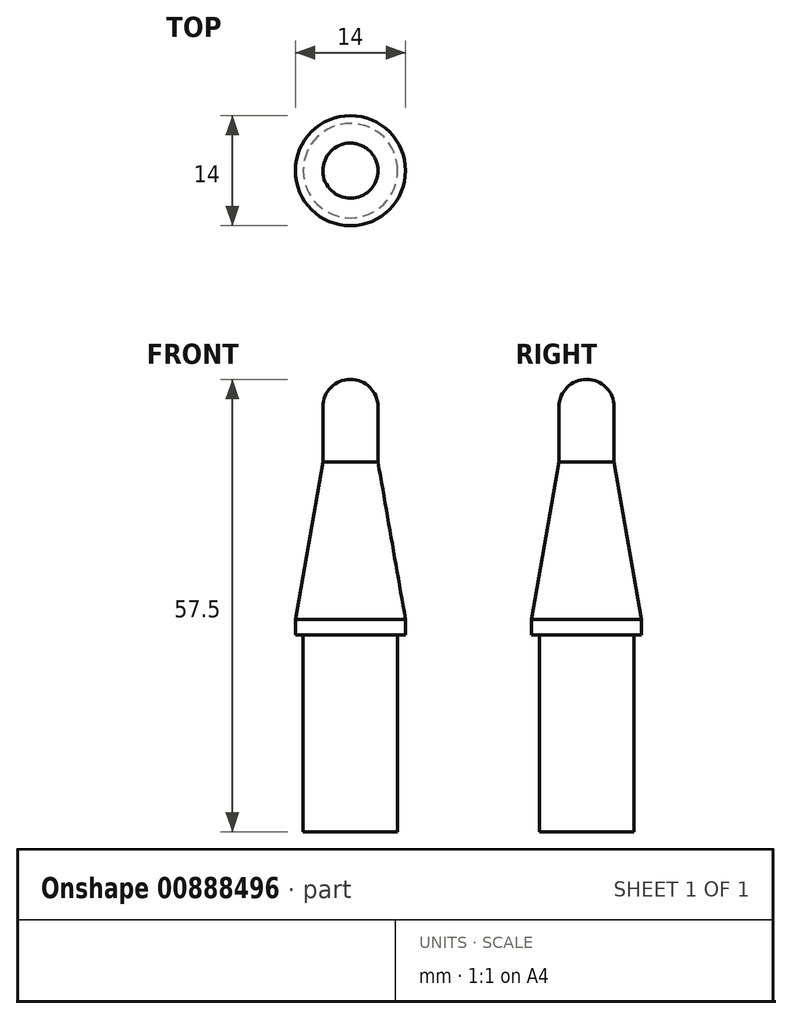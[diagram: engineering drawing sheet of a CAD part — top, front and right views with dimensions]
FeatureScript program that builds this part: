
annotation { "Feature Type Name" : "Feature", "Feature Type Description" : "" }
export const myFeature = defineFeature(function(context is Context, id is Id, definition is map)
    precondition{}
    {
        {
            var Q0;
            Q0=qCreatedBy(makeId("Top.planeOp"),FACE);
            var sketch = newSketch(context, id + "F0", { "sketchPlane" : qUnion([Q0])});
            skCircle(sketch, "E0", {"center": v(0, 0) * mm, "radius": 6 * mm});
            skSolve(sketch);
        }
        {
            var Q0;
            Q0 = qSketchRegion(id + "F0", true);
            extrude(context, id + "F1", {"entities" : qUnion([Q0]), "depth" : 25 * mm, "offsetDistance" : 25 * mm});
        }
        {
            var Q0;
            Q0=makeQuery(id+"F1.opExtrude","CAP_FACE",FACE,{"disambiguationData":[OSD([sQuery(id+"F0.wireOp",EDGE,"E0")])],"isStart":false});
            var sketch = newSketch(context, id + "F2", { "sketchPlane" : qUnion([Q0])});
            skCircle(sketch, "E1", {"center": v(0, 0) * mm, "radius": 7 * mm});
            skSolve(sketch);
        }
        {
            var Q0;
            Q0 = qSketchRegion(id + "F2", true);
            extrude(context, id + "F3", {"entities" : qUnion([Q0]), "operationType" : NewBodyOperationType.ADD, "depth" : 2 * mm, "offsetDistance" : 25 * mm});
        }
        {
            var Q0;
            Q0=makeQuery(id+"F3.opExtrude","CAP_FACE",FACE,{"disambiguationData":[OSD([sQuery(id+"F2.wireOp",EDGE,"E1")])],"isStart":false});
            cPlane(context, id + "F4", {"entities" : qUnion([Q0]), "cplaneType" : CPlaneType.OFFSET, "offset" : 20 * mm, "width" : 150 * mm, "height" : 150 * mm});
        }
        {
            var Q0;
            Q0=qCreatedBy(id+"F4.planeOp",FACE);
            var sketch = newSketch(context, id + "F5", { "sketchPlane" : qUnion([Q0])});
            skCircle(sketch, "E2", {"center": v(0, 0) * mm, "radius": 3.5 * mm});
            skSolve(sketch);
        }
        {
            var Q1;
            Q1=makeQuery(id+"F3.opExtrude","CAP_FACE",FACE,{"disambiguationData":[OSD([sQuery(id+"F2.wireOp",EDGE,"E1")])],"isStart":false});
            var Q2;
            Q2=makeQuery(id+"F5.imprint","IMPRINT",FACE,{"disambiguationData":[TD([[makeQuery(id+"F5.imprint","IMPRINT",EDGE,{"derivedFrom":sQuery(id+"F5.wireOp",EDGE,"E2")}),1.0]])]});
            loft(context, id + "F6", {"operationType" : NewBodyOperationType.ADD, "sheetProfilesArray" : [{ "sheetProfileEntities" : qUnion([Q1]) }, { "sheetProfileEntities" : qUnion([Q2]) }]});
        }
        {
            var Q0;
            Q0=makeQuery(id+"F6.opLoft","CAP_FACE",FACE,{"disambiguationData":[OSD([makeQuery(id+"F5.imprint","IMPRINT",FACE,{"disambiguationData":[TD([[makeQuery(id+"F5.imprint","IMPRINT",EDGE,{"derivedFrom":sQuery(id+"F5.wireOp",EDGE,"E2")}),1.0]])]})])],"isStart":true});
            extrude(context, id + "F7", {"entities" : qUnion([Q0]), "operationType" : NewBodyOperationType.ADD, "depth" : 7 * mm, "offsetDistance" : 25 * mm});
        }
        {
            var Q0;
            Q0=makeQuery(id+"F7.opExtrude","CAP_FACE",FACE,{"disambiguationData":[OSD([makeQuery(id+"F5.imprint","IMPRINT",FACE,{"disambiguationData":[TD([[makeQuery(id+"F5.imprint","IMPRINT",EDGE,{"derivedFrom":sQuery(id+"F5.wireOp",EDGE,"E2")}),1.0]])]})])],"isStart":false});
            var sketch = newSketch(context, id + "F8", { "sketchPlane" : qUnion([Q0])});
            skLineSegment(sketch, "E3", {"start": v(0, 0) * mm, "end": v(0.4, -3.48) * mm});
            skLineSegment(sketch, "E4", {"start": v(0, 0) * mm, "end": v(-0.4, 3.48) * mm});
            skSolve(sketch);
        }
        {
            var Q0;
            {var subQ0=sQuery(id+"F8.wireOp",EDGE,"E3");Q0=makeQuery(id+"F8.imprint","IMPRINT",FACE,{"disambiguationData":[TD([[makeQuery(id+"F8.imprint","IMPRINT",EDGE,{"derivedFrom":subQ0}),-1.0]])]});}
            var Q1;
            Q1=sQuery(id+"F8.wireOp",EDGE,"E3");
            revolve(context, id + "F9", {"operationType" : NewBodyOperationType.ADD, "surfaceOperationType" : NewSurfaceOperationType.NEW, "entities" : qUnion([Q0]), "axis" : qUnion([Q1]), "revolveType" : RevolveType.FULL});
        }
    });
